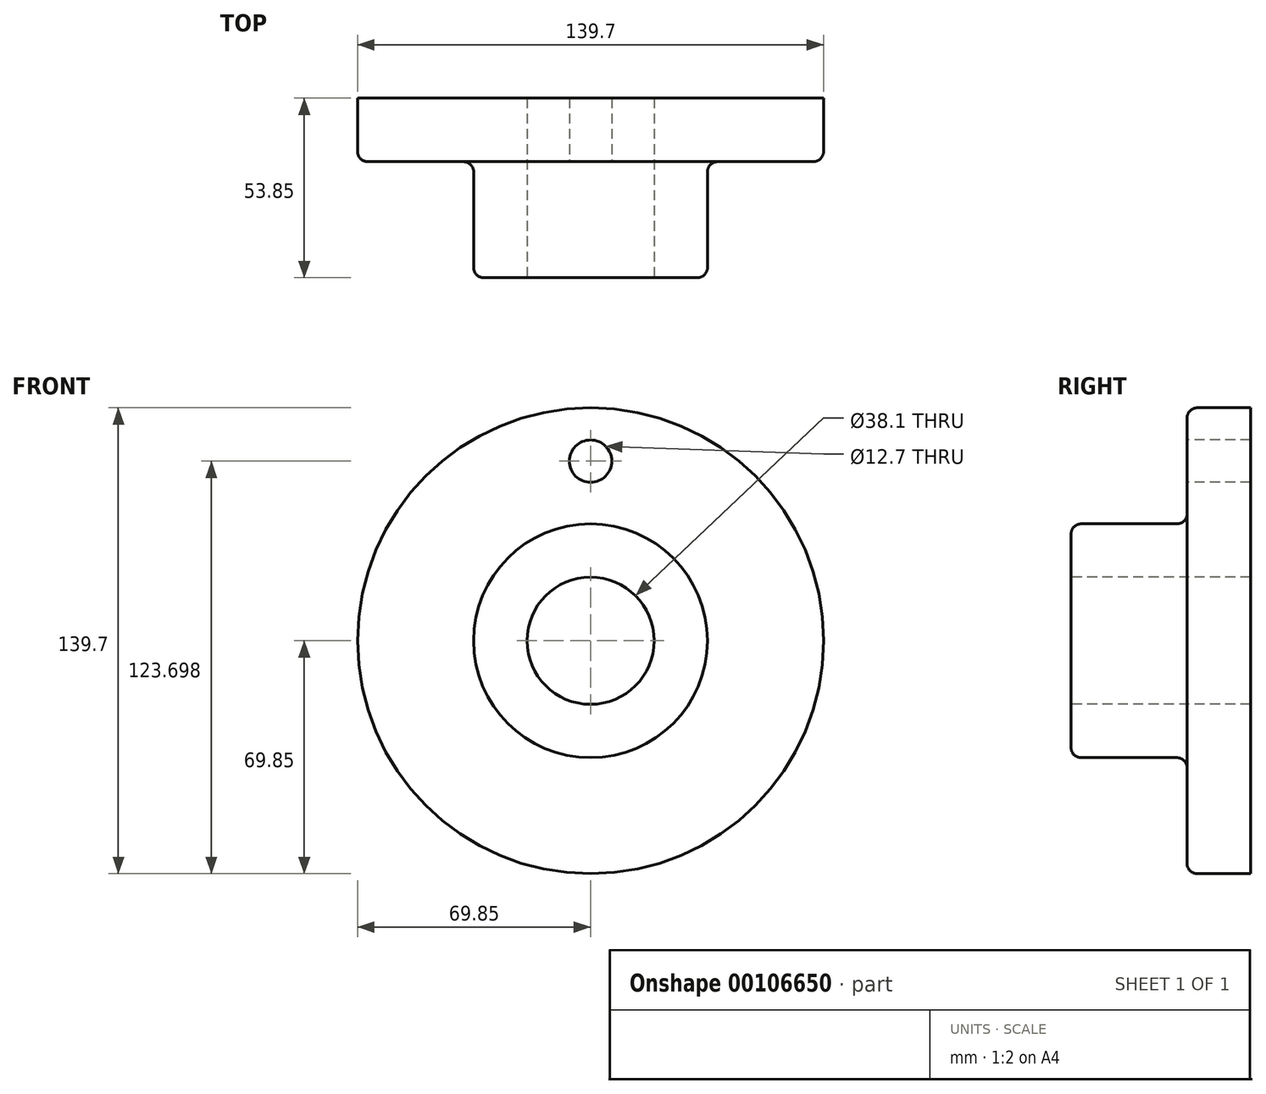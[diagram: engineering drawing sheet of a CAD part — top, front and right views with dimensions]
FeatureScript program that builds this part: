
annotation { "Feature Type Name" : "Feature", "Feature Type Description" : "" }
export const myFeature = defineFeature(function(context is Context, id is Id, definition is map)
    precondition{}
    {
        {
            var Q0;
            Q0=qCreatedBy(makeId("Right.planeOp"),FACE);
            var sketch = newSketch(context, id + "F0", { "sketchPlane" : qUnion([Q0])});
            skLineSegment(sketch, "E0", {"start": v(-109.66, 0) * mm, "end": v(108.39, 0) * mm, "construction": true});
            skLineSegment(sketch, "E1", {"start": v(0, 19.05) * mm, "end": v(-53.85, 19.05) * mm});
            skLineSegment(sketch, "E2", {"start": v(-53.85, 19.05) * mm, "end": v(-53.85, 35.05) * mm});
            skLineSegment(sketch, "E3", {"start": v(-53.85, 35.05) * mm, "end": v(-19.05, 35.05) * mm});
            skLineSegment(sketch, "E4", {"start": v(-19.05, 35.05) * mm, "end": v(-19.05, 69.85) * mm});
            skLineSegment(sketch, "E5", {"start": v(-19.05, 69.85) * mm, "end": v(0, 69.85) * mm});
            skLineSegment(sketch, "E6", {"start": v(0, 69.85) * mm, "end": v(0, 19.05) * mm});
            skSolve(sketch);
        }
        {
            var Q0;
            Q0 = qSketchRegion(id + "F0", true);
            var Q1;
            Q1=sQuery(id+"F0.wireOp",EDGE,"E0");
            revolve(context, id + "F1", {"entities" : qUnion([Q0]), "axis" : qUnion([Q1]), "revolveType" : RevolveType.FULL});
        }
        {
            var Q0;
            Q0=makeQuery(id+"F1.opRevolve","SWEPT_FACE",FACE,{"disambiguationData":[OSD([sQuery(id+"F0.wireOp",EDGE,"E4")])]});
            var sketch = newSketch(context, id + "F2", { "sketchPlane" : qUnion([Q0])});
            skCircle(sketch, "E7", {"center": v(0, 53.85) * mm, "radius": 6.35 * mm});
            skSolve(sketch);
        }
        {
            var Q0;
            Q0=makeQuery(id+"F2.imprint","IMPRINT",FACE,{"disambiguationData":[TD([[makeQuery(id+"F2.imprint","IMPRINT",EDGE,{"derivedFrom":sQuery(id+"F2.wireOp",EDGE,"E7")}),1.0]])]});
            extrude(context, id + "F3", {"entities" : qUnion([Q0]), "operationType" : NewBodyOperationType.REMOVE, "endBound" : BoundingType.THROUGH_ALL, "oppositeDirection" : true, "depth" : 25.4 * mm});
        }
        {
            var Q0;
            Q0=makeQuery(id+"F1.opRevolve","SWEPT_EDGE",EDGE,{"disambiguationData":[OSD([sQuery(id+"F0.wireOp",EDGE,"E4"),sQuery(id+"F0.wireOp",EDGE,"E5")])]});
            var Q1;
            Q1=makeQuery(id+"F1.opRevolve","SWEPT_EDGE",EDGE,{"disambiguationData":[OSD([sQuery(id+"F0.wireOp",EDGE,"E2"),sQuery(id+"F0.wireOp",EDGE,"E3")])]});
            var Q2;
            Q2=makeQuery(id+"F1.opRevolve","SWEPT_EDGE",EDGE,{"disambiguationData":[OSD([sQuery(id+"F0.wireOp",EDGE,"E3"),sQuery(id+"F0.wireOp",EDGE,"E4")])]});
            fillet(context, id + "F4", {"entities" : qUnion([Q0, Q1, Q2]), "radius" : 3.05 * mm, "tangentPropagation" : true, "allowEdgeOverflow" : false});
        }
    });
